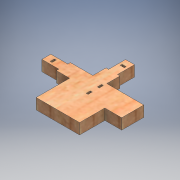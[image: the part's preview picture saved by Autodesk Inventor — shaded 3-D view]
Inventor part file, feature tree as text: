
AUTODESK INVENTOR PART (.ipt)
format: ipt  version: 2016 (Build 200138000, 138)  size: 201,216 bytes
history: native  units: mm
features: extrude x1, sketch x1
ambient origin geometry x8: Origin, YZ Plane, XZ Plane, XY Plane, X Axis, Y Axis, Z Axis, Center Point
bodies: Body1 (feature_tree)
feature tree (2):
  extrude  "Extrusion2"  Depth=10.1mm
  sketch  "Sketch1"  dims[d4=1.5mm d26=10.1mm d27=5.294635mm d31=2.5mm d32=1.1mm d35=5.5mm d41=1.1mm d42=2.5mm d72=17.5mm d89=6.39mm d90=0.0mm d99=5.5mm d103=12.0mm d104=10.0mm d105=13.147317mm d106=2.0mm d108=15.0mm d124=12.0mm d125=7.852683mm]
